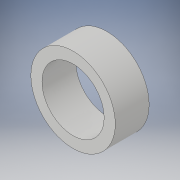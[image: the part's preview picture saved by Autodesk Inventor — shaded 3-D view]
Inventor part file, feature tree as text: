
AUTODESK INVENTOR PART (.ipt)
format: ipt  version: 2019 (Build 230136000, 136)  size: 102,912 bytes
history: native  units: mm
features: extrude x2, sketch x2
ambient origin geometry x8: Origin, YZ Plane, XZ Plane, XY Plane, X Axis, Y Axis, Z Axis, Center Point
bodies: Solid1 (feature_tree)
feature tree (4):
  extrude  "Extrusion1"  Depth=20.245mm TaperAngle=0.0deg
  extrude  "Extrusion2"  Depth=20.245mm TaperAngle=0.0deg
  sketch  "Sketch1"  dims[d0=50.42mm d1=20.245mm d2=0.0mm]
  sketch  "Sketch2"  dims[d3=37.14mm d4=20.245mm d5=0.0mm]
